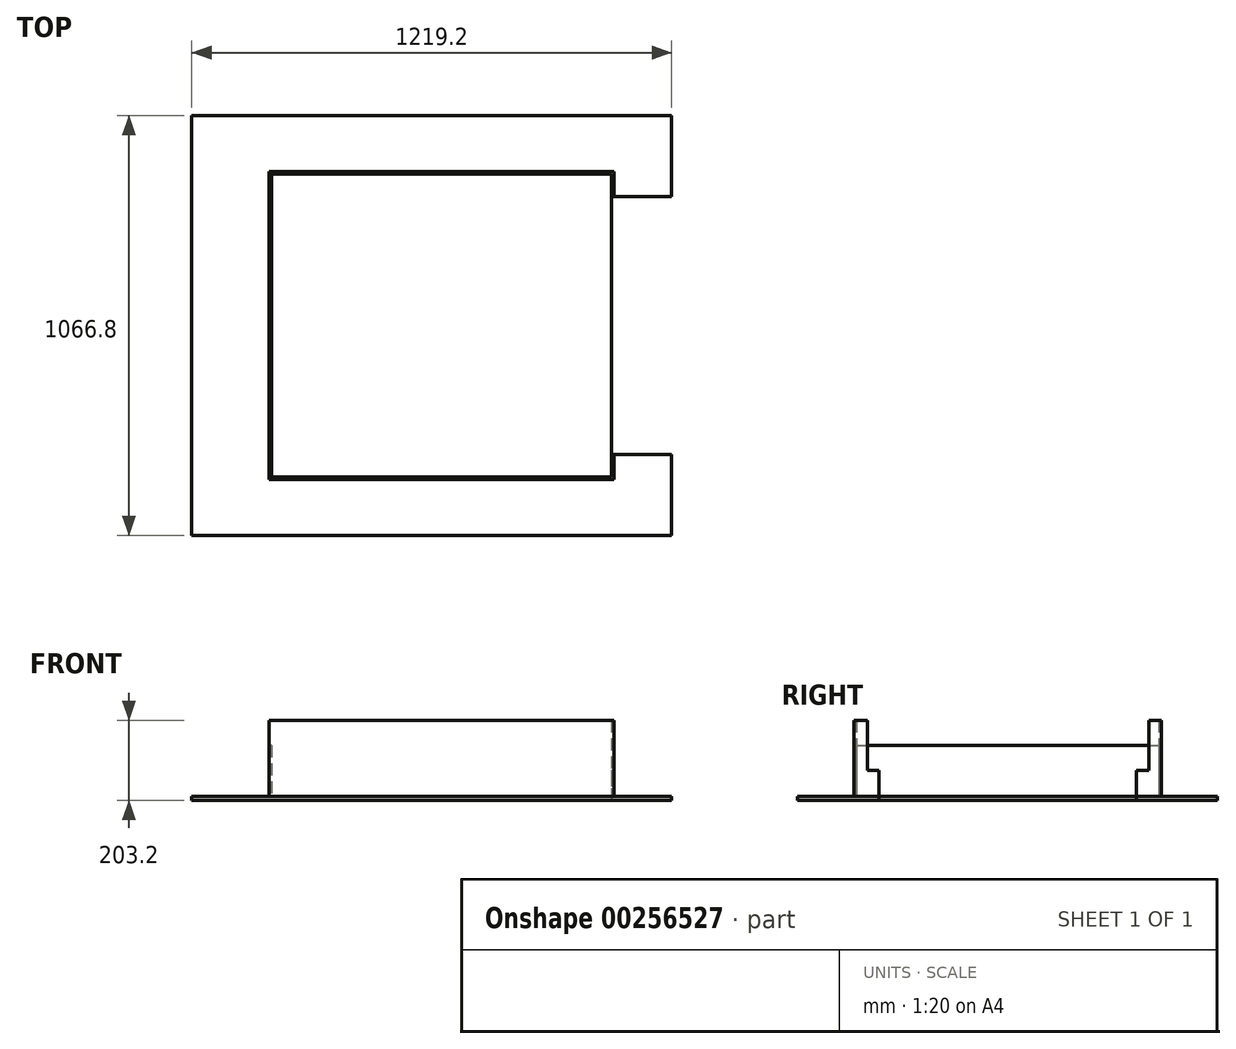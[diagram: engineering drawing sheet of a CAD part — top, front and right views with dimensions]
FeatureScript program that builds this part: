
annotation { "Feature Type Name" : "Feature", "Feature Type Description" : "" }
export const myFeature = defineFeature(function(context is Context, id is Id, definition is map)
    precondition{}
    {
        {
            var Q0;
            Q0=qCreatedBy(makeId("Top.planeOp"),FACE);
            var sketch = newSketch(context, id + "F0", { "sketchPlane" : qUnion([Q0])});
            skLineSegment(sketch, "E0.bottom", {"start": v(609.6, -533.4) * mm, "end": v(-609.6, -533.4) * mm});
            skLineSegment(sketch, "E0.left", {"start": v(609.6, -533.4) * mm, "end": v(609.6, -327.28) * mm});
            skLineSegment(sketch, "E0.right", {"start": v(-609.6, -533.4) * mm, "end": v(-609.6, 0) * mm});
            skPoint(sketch, "E0.middle", {"position": v(0, 0) * mm});
            skLineSegment(sketch, "E1", {"start": v(457.2, -327.28) * mm, "end": v(609.6, -327.28) * mm});
            skPoint(sketch, "E2", {"position": v(457.2, -228.6) * mm});
            skLineSegment(sketch, "E3", {"start": v(457.2, -390.78) * mm, "end": v(-412.75, -390.78) * mm});
            skPoint(sketch, "E4", {"position": v(457.2, -384.43) * mm});
            skLineSegment(sketch, "E5", {"start": v(457.2, -384.43) * mm, "end": v(-406.4, -384.43) * mm});
            skPoint(sketch, "E6", {"position": v(-406.4, -384.43) * mm});
            skLineSegment(sketch, "E7", {"start": v(-406.4, -384.43) * mm, "end": v(-406.4, 0) * mm});
            skLineSegment(sketch, "E8", {"start": v(-412.75, -390.78) * mm, "end": v(-412.75, 0) * mm});
            skLineSegment(sketch, "E9.trimOffspring", {"start": v(457.2, 0) * mm, "end": v(457.2, -327.28) * mm});
            skPoint(sketch, "E10.trimOffspring.end.orphan", {"position": v(-609.6, -384.43) * mm});
            skPoint(sketch, "E11.trimOffspring.end.orphan", {"position": v(457.2, -533.4) * mm});
            skPoint(sketch, "E12.MirrorP", {"position": v(-406.4, 384.43) * mm});
            skPoint(sketch, "E13.MirrorP", {"position": v(457.2, 384.43) * mm});
            skPoint(sketch, "E14.MirrorP", {"position": v(457.2, 390.78) * mm});
            skLineSegment(sketch, "E15.MirrorCS", {"start": v(457.2, 384.43) * mm, "end": v(-406.4, 384.43) * mm});
            skLineSegment(sketch, "E16.MirrorCS", {"start": v(-406.4, 384.43) * mm, "end": v(-406.4, 0) * mm});
            skLineSegment(sketch, "E17.MirrorCS", {"start": v(-609.6, 533.4) * mm, "end": v(-609.6, 0) * mm});
            skLineSegment(sketch, "E18.MirrorCS", {"start": v(457.2, 0) * mm, "end": v(457.2, 327.28) * mm});
            skLineSegment(sketch, "E19.MirrorCS", {"start": v(609.6, 533.4) * mm, "end": v(-609.6, 533.4) * mm});
            skPoint(sketch, "E20.MirrorP", {"position": v(457.2, 533.4) * mm});
            skLineSegment(sketch, "E21.MirrorCS", {"start": v(-412.75, 390.78) * mm, "end": v(-412.75, 0) * mm});
            skLineSegment(sketch, "E22.MirrorCS", {"start": v(457.2, 390.78) * mm, "end": v(-412.75, 390.78) * mm});
            skLineSegment(sketch, "E23.MirrorCS", {"start": v(457.2, 327.28) * mm, "end": v(609.6, 327.28) * mm});
            skLineSegment(sketch, "E24.MirrorCS", {"start": v(609.6, 533.4) * mm, "end": v(609.6, 327.28) * mm});
            skLineSegment(sketch, "E25", {"start": v(457.2, 384.43) * mm, "end": v(457.2, 327.28) * mm});
            skPoint(sketch, "E26", {"position": v(457.2, 359.03) * mm});
            skPoint(sketch, "E27", {"position": v(463.55, 327.28) * mm});
            skLineSegment(sketch, "E28", {"start": v(463.55, 327.28) * mm, "end": v(463.55, 390.78) * mm});
            skLineSegment(sketch, "E29", {"start": v(457.2, 390.78) * mm, "end": v(463.55, 390.78) * mm});
            skLineSegment(sketch, "E30", {"start": v(457.2, -327.28) * mm, "end": v(457.2, -384.43) * mm});
            skPoint(sketch, "E31", {"position": v(463.55, -327.28) * mm});
            skLineSegment(sketch, "E32", {"start": v(463.55, -327.28) * mm, "end": v(463.55, -390.78) * mm});
            skLineSegment(sketch, "E33", {"start": v(457.2, -390.78) * mm, "end": v(463.55, -390.78) * mm});
            skPoint(sketch, "E34", {"position": v(457.2, -355.85) * mm});
            skLineSegment(sketch, "E35", {"start": v(457.2, -355.85) * mm, "end": v(463.55, -355.85) * mm});
            skLineSegment(sketch, "E36", {"start": v(457.2, 359.03) * mm, "end": v(463.55, 359.03) * mm});
            skLineSegment(sketch, "E37", {"start": v(-406.4, 384.43) * mm, "end": v(-412.75, 384.43) * mm});
            skLineSegment(sketch, "E38", {"start": v(-406.4, -384.43) * mm, "end": v(-412.75, -384.43) * mm});
            skSolve(sketch);
        }
        {
            var Q0;
            Q0 = qSketchRegion(id + "F0", true);
            extrude(context, id + "F1", {"entities" : qUnion([Q0]), "depth" : 9.52 * mm});
        }
        {
            var Q0;
            {var subQ5=sQuery(id+"F0.wireOp",EDGE,"E36");Q0=makeQuery(id+"F0.imprint","IMPRINT",FACE,{"disambiguationData":[TD([[makeQuery(id+"F0.imprint","IMPRINT",EDGE,{"derivedFrom":subQ5}),-1.0]])]});}
            var Q1;
            {var subQ5=sQuery(id+"F0.wireOp",EDGE,"E35");Q1=makeQuery(id+"F0.imprint","IMPRINT",FACE,{"disambiguationData":[TD([[makeQuery(id+"F0.imprint","IMPRINT",EDGE,{"derivedFrom":subQ5}),1.0]])]});}
            extrude(context, id + "F2", {"entities" : qUnion([Q0, Q1]), "operationType" : NewBodyOperationType.ADD, "depth" : 76.2 * mm});
        }
        {
            var Q0;
            Q0=makeQuery(id+"F0.imprint","IMPRINT",FACE,{"disambiguationData":[TD([[makeQuery(id+"F0.imprint","IMPRINT",EDGE,{"derivedFrom":sQuery(id+"F0.wireOp",EDGE,"E3")}),-1.0]])]});
            extrude(context, id + "F3", {"entities" : qUnion([Q0]), "operationType" : NewBodyOperationType.ADD, "depth" : 203.2 * mm});
        }
        {
            var Q0;
            Q0=makeQuery(id+"F0.imprint","IMPRINT",FACE,{"disambiguationData":[TD([[makeQuery(id+"F0.imprint","IMPRINT",EDGE,{"derivedFrom":sQuery(id+"F0.wireOp",EDGE,"E7")}),1.0]])]});
            extrude(context, id + "F4", {"entities" : qUnion([Q0]), "operationType" : NewBodyOperationType.ADD, "depth" : 139.7 * mm});
        }
        {
            var Q0;
            {var subQ1=sQuery(id+"F0.wireOp",EDGE,"E15.MirrorCS");Q0=makeQuery(id+"F0.imprint","IMPRINT",FACE,{"disambiguationData":[TD([[makeQuery(id+"F0.imprint","IMPRINT",EDGE,{"derivedFrom":subQ1}),-1.0]])]});}
            extrude(context, id + "F5", {"entities" : qUnion([Q0]), "operationType" : NewBodyOperationType.ADD, "depth" : 203.2 * mm});
        }
    });
